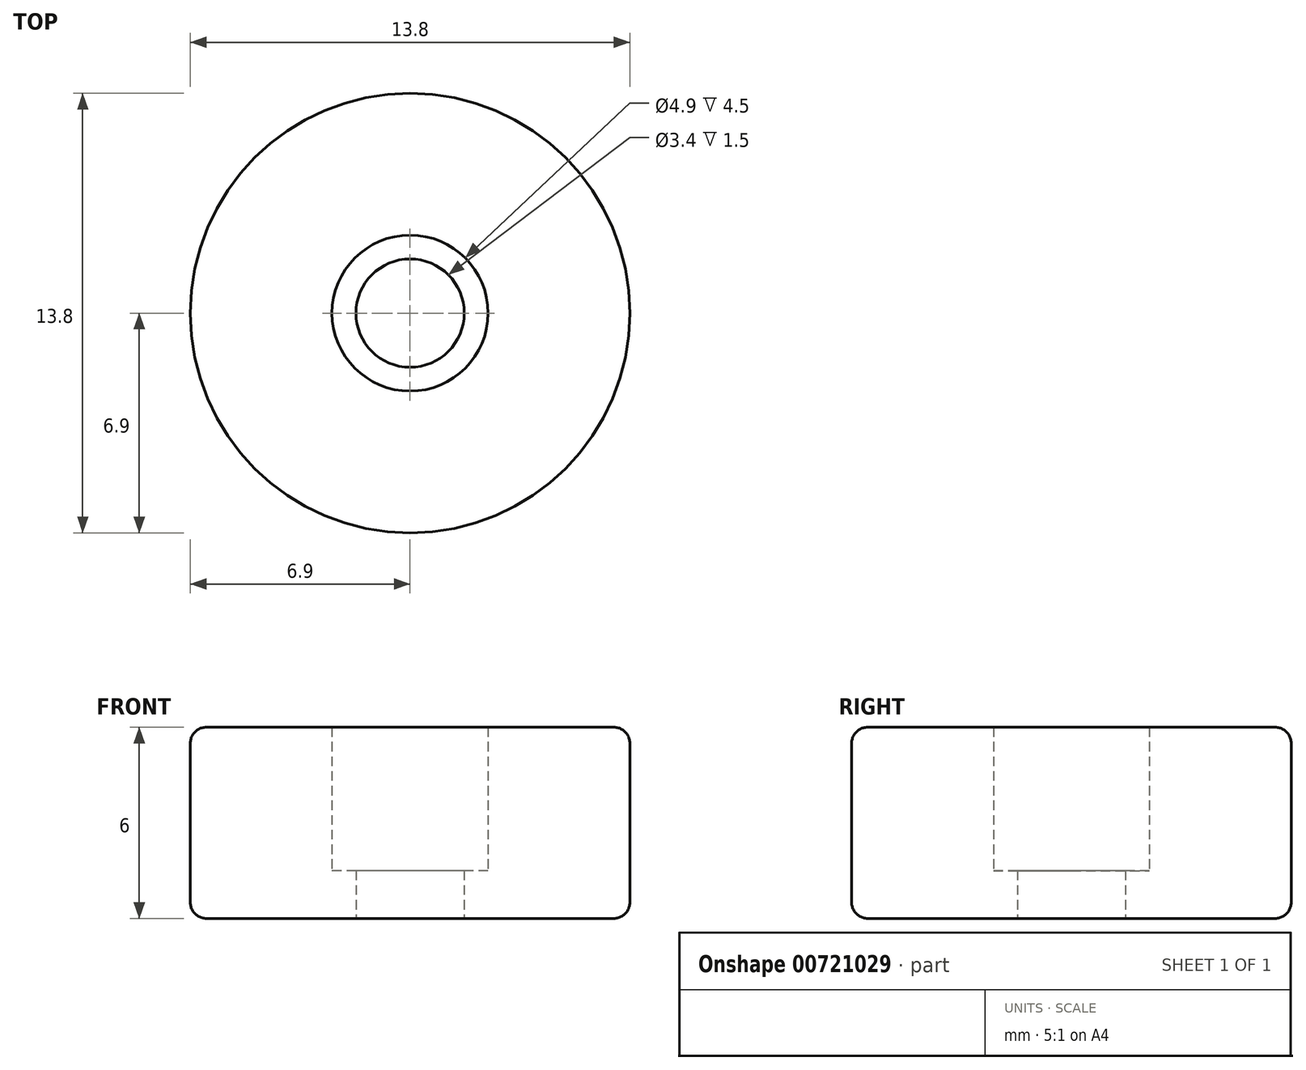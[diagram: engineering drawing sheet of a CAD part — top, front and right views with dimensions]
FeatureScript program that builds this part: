
annotation { "Feature Type Name" : "Feature", "Feature Type Description" : "" }
export const myFeature = defineFeature(function(context is Context, id is Id, definition is map)
    precondition{}
    {
        {
            var Q0;
            Q0=qCreatedBy(makeId("Top.planeOp"),FACE);
            var sketch = newSketch(context, id + "F0", { "sketchPlane" : qUnion([Q0])});
            skCircle(sketch, "E0", {"center": v(0, 0) * mm, "radius": 1.7 * mm});
            skCircle(sketch, "E1", {"center": v(0, 0) * mm, "radius": 6.9 * mm});
            skCircle(sketch, "E2", {"center": v(0, 0) * mm, "radius": 2.45 * mm});
            skSolve(sketch);
        }
        {
            var Q0;
            Q0=makeQuery(id+"F0.imprint","IMPRINT",FACE,{"disambiguationData":[TD([[makeQuery(id+"F0.imprint","IMPRINT",EDGE,{"derivedFrom":sQuery(id+"F0.wireOp",EDGE,"E1")}),1.0]])]});
            extrude(context, id + "F1", {"entities" : qUnion([Q0]), "depth" : 6 * mm, "offsetDistance" : 25 * mm});
        }
        {
            var Q0;
            Q0=makeQuery(id+"F0.imprint","IMPRINT",FACE,{"disambiguationData":[TD([[makeQuery(id+"F0.imprint","IMPRINT",EDGE,{"derivedFrom":sQuery(id+"F0.wireOp",EDGE,"E0")}),-1.0]])]});
            extrude(context, id + "F2", {"entities" : qUnion([Q0]), "operationType" : NewBodyOperationType.ADD, "depth" : 1.5 * mm, "offsetDistance" : 25 * mm});
        }
        {
            var Q0;
            Q0=makeQuery(id+"F1.opExtrude","CAP_EDGE",EDGE,{"disambiguationData":[OSD([sQuery(id+"F0.wireOp",EDGE,"E1")])],"isStart":false});
            var Q1;
            Q1=makeQuery(id+"F1.opExtrude","CAP_EDGE",EDGE,{"disambiguationData":[OSD([sQuery(id+"F0.wireOp",EDGE,"E1")])],"isStart":true});
            fillet(context, id + "F3", {"entities" : qUnion([Q0, Q1]), "radius" : 0.5 * mm, "tangentPropagation" : true, "allowEdgeOverflow" : false});
        }
    });
